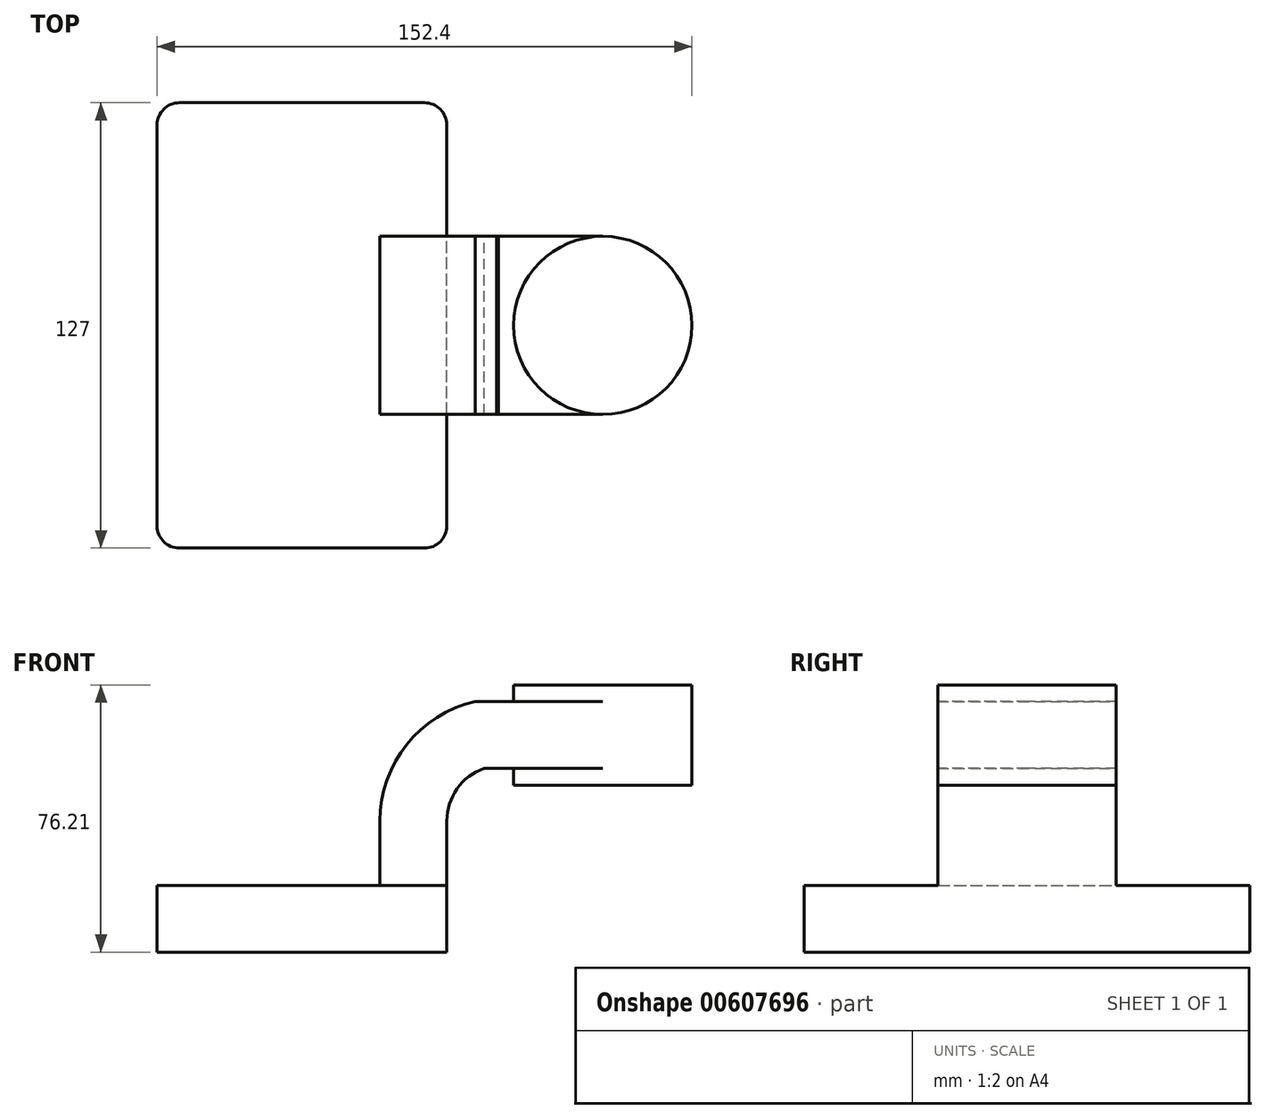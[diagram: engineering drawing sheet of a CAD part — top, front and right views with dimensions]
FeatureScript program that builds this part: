
annotation { "Feature Type Name" : "Feature", "Feature Type Description" : "" }
export const myFeature = defineFeature(function(context is Context, id is Id, definition is map)
    precondition{}
    {
        {
            var Q0;
            Q0=qCreatedBy(makeId("Front.planeOp"),FACE);
            var sketch = newSketch(context, id + "F0", { "sketchPlane" : qUnion([Q0])});
            skLineSegment(sketch, "E0.bottom", {"start": v(-41.28, -9.53) * mm, "end": v(41.28, -9.53) * mm});
            skLineSegment(sketch, "E0.top", {"start": v(-41.28, 9.53) * mm, "end": v(41.28, 9.53) * mm});
            skLineSegment(sketch, "E0.left", {"start": v(-41.28, -9.53) * mm, "end": v(-41.28, 9.53) * mm});
            skLineSegment(sketch, "E0.right", {"start": v(41.28, -9.53) * mm, "end": v(41.28, 9.53) * mm});
            skPoint(sketch, "E0.middle", {"position": v(0, 0) * mm});
            skLineSegment(sketch, "E1.bottom", {"start": v(60.32, 38.1) * mm, "end": v(111.12, 38.1) * mm});
            skLineSegment(sketch, "E1.top", {"start": v(60.32, 66.67) * mm, "end": v(111.12, 66.67) * mm});
            skLineSegment(sketch, "E1.left", {"start": v(60.32, 38.1) * mm, "end": v(60.32, 66.67) * mm});
            skLineSegment(sketch, "E1.right", {"start": v(111.12, 38.1) * mm, "end": v(111.12, 66.67) * mm});
            skPoint(sketch, "E1.middle", {"position": v(85.72, 52.39) * mm});
            skLineSegment(sketch, "E2", {"start": v(41.27, 9.53) * mm, "end": v(41.27, 27.89) * mm});
            skArc(sketch, "E3", {"start": v(41.27, 27.89) * mm, "mid": v(44.2, 37.08) * mm, "end": v(51.92, 42.88) * mm});
            skLineSegment(sketch, "E4", {"start": v(51.92, 42.88) * mm, "end": v(85.72, 42.88) * mm});
            skPoint(sketch, "E4.endSnap0", {"position": v(85.72, 38.1) * mm});
            skLineSegment(sketch, "E5.0", {"start": v(49.33, 61.93) * mm, "end": v(85.72, 61.93) * mm});
            skArc(sketch, "E5.1", {"start": v(22.23, 27.89) * mm, "mid": v(29.83, 49.64) * mm, "end": v(49.33, 61.93) * mm});
            skLineSegment(sketch, "E5.2", {"start": v(22.22, 9.53) * mm, "end": v(22.22, 27.89) * mm});
            skLineSegment(sketch, "E6", {"start": v(85.72, 38.1) * mm, "end": v(85.72, 61.93) * mm});
            skLineSegment(sketch, "E7", {"start": v(85.72, 61.93) * mm, "end": v(85.72, 66.67) * mm});
            skFitSpline(sketch, "E8", {"points": [v(-41.28, 9.53) * mm, v(49.33, 61.93) * mm, v(56.02, 61.93) * mm, v(55.39, 61.93) * mm], "startDerivative": vector(-0.79, 95.5) * mm, "endDerivative": vector(-6.1, -0.15) * mm});
            skSolve(sketch);
        }
        {
            var Q0;
            Q0=makeQuery(id+"F0.imprint","IMPRINT",FACE,{"disambiguationData":[TD([[makeQuery(id+"F0.imprint","IMPRINT",EDGE,{"derivedFrom":sQuery(id+"F0.wireOp",EDGE,"E0.bottom")}),1.0]])]});
            extrude(context, id + "F1", {"entities" : qUnion([Q0]), "endBound" : BoundingType.SYMMETRIC, "depth" : 127 * mm, "offsetDistance" : 25.4 * mm});
        }
        {
            var Q0;
            {var subQ12=sQuery(id+"F0.wireOp",EDGE,"E2");Q0=makeQuery(id+"F0.imprint","IMPRINT",FACE,{"disambiguationData":[TD([[makeQuery(id+"F0.imprint","IMPRINT",EDGE,{"derivedFrom":subQ12}),1.0]])]});}
            var Q1;
            {var subQ0=sQuery(id+"F0.wireOp",EDGE,"E4");var subQ1=sQuery(id+"F0.wireOp",EDGE,"E1.left");var subQ2=makeQuery(id+"F0.imprint","INTERSECT",VERTEX,{"derivedFrom":[subQ1,subQ0]});Q1=makeQuery(id+"F0.imprint","IMPRINT",FACE,{"disambiguationData":[TD([[makeQuery(id+"F0.imprint","IMPRINT",EDGE,{"disambiguationData":[TD([[subQ2,-1.0]])],"derivedFrom":subQ1}),-1.0]])]});}
            extrude(context, id + "F2", {"entities" : qUnion([Q0, Q1]), "operationType" : NewBodyOperationType.ADD, "endBound" : BoundingType.SYMMETRIC, "depth" : 50.8 * mm, "offsetDistance" : 25.4 * mm});
        }
        {
            var Q0;
            {var subQ4=sQuery(id+"F0.wireOp",EDGE,"E5.1");Q0=makeQuery(id+"F0.imprint","IMPRINT",FACE,{"disambiguationData":[TD([[makeQuery(id+"F0.imprint","IMPRINT",EDGE,{"derivedFrom":subQ4}),1.0]])]});}
            extrude(context, id + "F3", {"entities" : qUnion([Q0]), "operationType" : NewBodyOperationType.ADD, "endBound" : BoundingType.SYMMETRIC, "depth" : 15.88 * mm, "offsetDistance" : 25.4 * mm});
        }
        {
            var Q0;
            {var subQ0=sQuery(id+"F0.wireOp",EDGE,"E1.right");Q0=makeQuery(id+"F0.imprint","IMPRINT",FACE,{"disambiguationData":[TD([[makeQuery(id+"F0.imprint","IMPRINT",EDGE,{"derivedFrom":subQ0}),1.0]])]});}
            var Q1;
            Q1=sQuery(id+"F0.wireOp",EDGE,"E6");
            revolve(context, id + "F4", {"operationType" : NewBodyOperationType.ADD, "entities" : qUnion([Q0]), "axis" : qUnion([Q1]), "revolveType" : RevolveType.FULL});
        }
        {
            var Q0;
            Q0=makeQuery(id+"F1.opExtrude","CAP_EDGE",EDGE,{"disambiguationData":[OSD([sQuery(id+"F0.wireOp",EDGE,"E0.left")])],"isStart":false});
            var Q1;
            Q1=makeQuery(id+"F1.opExtrude","CAP_EDGE",EDGE,{"disambiguationData":[OSD([sQuery(id+"F0.wireOp",EDGE,"E0.right")])],"isStart":false});
            var Q2;
            Q2=makeQuery(id+"F1.opExtrude","CAP_EDGE",EDGE,{"disambiguationData":[OSD([sQuery(id+"F0.wireOp",EDGE,"E0.right")])],"isStart":true});
            var Q3;
            Q3=makeQuery(id+"F1.opExtrude","CAP_EDGE",EDGE,{"disambiguationData":[OSD([sQuery(id+"F0.wireOp",EDGE,"E0.left")])],"isStart":true});
            fillet(context, id + "F5", {"entities" : qUnion([Q0, Q1, Q2, Q3]), "radius" : 6.35 * mm, "tangentPropagation" : true, "allowEdgeOverflow" : false});
        }
    });
